# Revit family: Partition-Privada-Floor_Anchored-HPL_Series
name_source: partatom
category: Specialty Equipment
revit_build: Autodesk Revit 2016 (Build: 20150714_1515(x64)
units: mm (PartAtom-declared; Revit-internal decimal feet)

## family parameters
Cut with Voids When Loaded = No
Host = Face
OmniClass Number = 23.25.40.14.14.11
OmniClass Title = Toilet Compartments and Urinal Screens
Part Type = Normal
Room Calculation Point = No
Round Connector Dimension = Use Diameter
Shared = Yes

## types (5) — shared parameters
2 - Left Hinged Outswing = No
4" Clearance Option = Yes
9" Clearance Option = No
Assembly Code = C1010
Clearance Height = 4"
Corner Stall Constraint = 60"
Corner Stall Width = 60"
Default Elevation = 48"
Description = Privada Floor-Anchored Toilet Compartment with concealed frame and mounting brackets.
Door Height = 72"
Door Height Constraint = 72"
Door Panel = Yes
Exterior Finish = Laminate-Privada-Mission White
Hardware Material = Hardware-Privada-Stainless Steel Satin
Head Rail Length = 1 1/8"
Installation Type = Floor-Anchored
Interior Finish = Laminate-Privada-Mission White
Left Partition = No
Length = 60"
Manufacturer = Privada
Model = Privada Floor-Anchored Toilet Compartment
Overall Height = 77 1/8"
Partition Length Constraint = 60"
Price = Prices may vary. Please consult Manufacturer Representative for most up-to-date price list.
Product Documentation Link = http://www.privadapartitions.com
Product Page URL = http://www.privadapartitions.com
Right Stile Option = Yes
URL = http://www.privadapartitions.com
Warranty Information = 10 Year Warranty

## per-type parameters (varying)
| type | 1 - Left Hinged Inswing | 3 - Right Hinged Inswing | 4 - Right Hinged Outswing | Center Stall Constraint | Center Stall Option | Center Stall Width | Corner Option | Door Option | Door Width | Inswing Visibility | Left Stile Constraint | Left Stile Option | Left Stile Width | Right Partition | Right Side Corner | Right Stile Constraint | Right Stile Width | Stall Width Constraint |
| Left Corner Partition | No | Yes | No | 48" | No | 72" | Yes | 3 | 36" | No | 48" | Yes | 60" | Yes | No | 12" | 12" | 60" |
| Center Partition | Yes | No | No | 32" | Yes | 32" | No | 1 | 24" | Yes | 8" | No | 8" | Yes | No | 8" | 8" | 32" |
| Right Corner Partition | No | No | Yes | 48" | Yes | 72" | No | 4 | 36" | No | 12" | No | 12" | No | Yes | 48" | 60" | 72" |
| Right Alcove | Yes | No | No | 32" | Yes | 32" | No | 1 | 24" | Yes | 8" | No | 8" | No | No | 8" | 8" | 32" |
| Left Alcove | Yes | No | No | 32" | Yes | 32" | No | 1 | 24" | Yes | 8" | Yes | 8" | Yes | No | 8" | 8" | 32" |

## geometry (parser evidence)
native form markers: Sweep x5
no freeform markers — native parametric forms only
